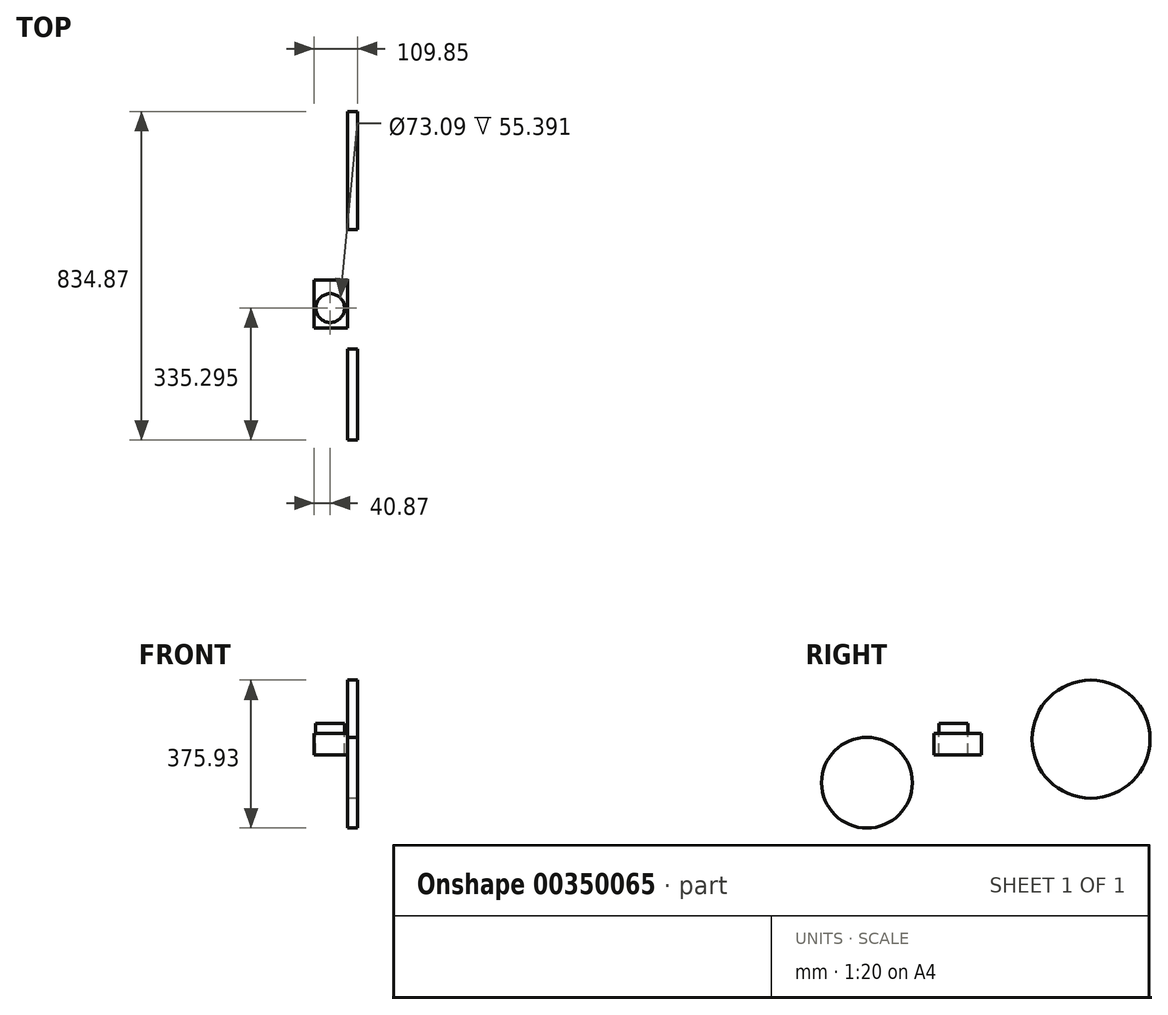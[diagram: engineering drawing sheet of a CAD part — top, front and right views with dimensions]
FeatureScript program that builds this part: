
annotation { "Feature Type Name" : "Feature", "Feature Type Description" : "" }
export const myFeature = defineFeature(function(context is Context, id is Id, definition is map)
    precondition{}
    {
        {
            var Q0;
            Q0=qCreatedBy(makeId("Front.planeOp"),FACE);
            var sketch = newSketch(context, id + "F0", { "sketchPlane" : qUnion([Q0])});
            skLineSegment(sketch, "E0.bottom", {"start": v(-40.87, 14.94) * mm, "end": v(43.98, 14.94) * mm});
            skLineSegment(sketch, "E0.top", {"start": v(-40.87, -40.45) * mm, "end": v(43.98, -40.45) * mm});
            skLineSegment(sketch, "E0.left", {"start": v(-40.87, 14.94) * mm, "end": v(-40.87, -40.45) * mm});
            skLineSegment(sketch, "E0.right", {"start": v(43.98, 14.94) * mm, "end": v(43.98, -40.45) * mm});
            skSolve(sketch);
        }
        {
            var Q0;
            Q0 = qSketchRegion(id + "F0", true);
            extrude(context, id + "F1", {"entities" : qUnion([Q0]), "depth" : 121.69 * mm});
        }
        {
            var Q0;
            Q0=makeQuery(id+"F1.opExtrude","SWEPT_FACE",FACE,{"disambiguationData":[OSD([sQuery(id+"F0.wireOp",EDGE,"E0.bottom")])]});
            var sketch = newSketch(context, id + "F2", { "sketchPlane" : qUnion([Q0])});
            skCircle(sketch, "E1", {"center": v(0, -71.38) * mm, "radius": 36.55 * mm});
            skSolve(sketch);
        }
        {
            var Q0;
            Q0 = qSketchRegion(id + "F2", true);
            extrude(context, id + "F3", {"entities" : qUnion([Q0]), "operationType" : NewBodyOperationType.REMOVE, "oppositeDirection" : true, "depth" : 102.4 * mm});
        }
        {
            var Q0;
            Q0 = qSketchRegion(id + "F2", true);
            extrude(context, id + "F4", {"entities" : qUnion([Q0]), "depth" : 25 * mm});
        }
        {
            var Q0;
            Q0=makeQuery(id+"F1.opExtrude","SWEPT_FACE",FACE,{"disambiguationData":[OSD([sQuery(id+"F0.wireOp",EDGE,"E0.right")])]});
            var sketch = newSketch(context, id + "F5", { "sketchPlane" : qUnion([Q0])});
            skCircle(sketch, "E2", {"center": v(-291.32, -110.57) * mm, "radius": 115.36 * mm});
            skCircle(sketch, "E3", {"center": v(278.19, 0) * mm, "radius": 150 * mm});
            skSolve(sketch);
        }
        {
            var Q0;
            Q0 = qSketchRegion(id + "F5", true);
            extrude(context, id + "F6", {"entities" : qUnion([Q0]), "operationType" : NewBodyOperationType.ADD, "depth" : 25 * mm});
        }
    });
